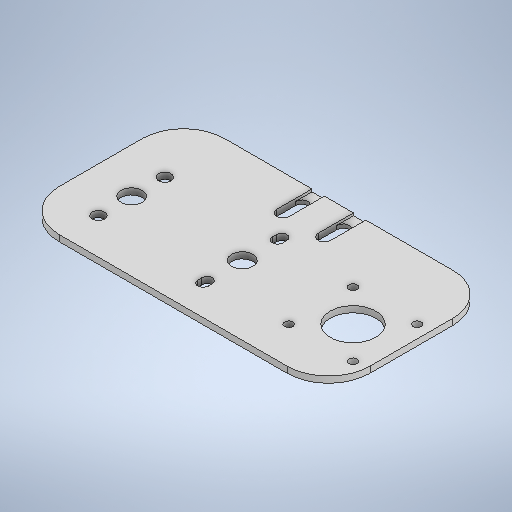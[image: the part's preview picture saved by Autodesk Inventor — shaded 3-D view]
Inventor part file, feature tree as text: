
AUTODESK INVENTOR PART (.ipt)
format: ipt  version: 2025.2 (Build 292293000, 293)  size: 341,504 bytes
history: native  units: mm
features: extrude x5, sketch x4, fillet x1
ambient origin geometry x8: Origin, YZ Plane, XZ Plane, XY Plane, X Axis, Y Axis, Z Axis, Center Point
bodies: Solid1 (feature_tree)
feature tree (10):
  extrude  "Extrusion1"  Depth=80.0mm
  sketch  "Sketch4"  dims[d2=3.0mm d3=0.0mm d14=20.0mm]
  extrude  "Extrusion3"  Depth=20.0mm
  extrude  "Extrusion4"  Depth=6.0mm
  extrude  "Extrusion5"  Depth=5.0mm
  extrude  "Extrusion6"  Depth=5.0mm
  fillet  "Fillet1"  Radius=3.0mm
  sketch  "Sketch1"  dims[d0=150.0mm d1=80.0mm]
  sketch  "Sketch5"  dims[d15=20.0mm d16=6.0mm]
  sketch  "Sketch6"  dims[d17=6.0mm d18=5.0mm d19=5.0mm d20=3.0mm d21=3.0mm d22=3.0mm d23=3.0mm d24=0.0mm d25=0.0mm d26=25.0mm d36=0.0mm d37=0.0mm d38=1.2mm d39=0.0mm d49=150.0mm d50=43.2mm d51=43.2mm d52=22.0mm d53=31.0mm d54=31.0mm d55=4.0mm d56=4.0mm d57=4.0mm d58=4.0mm d59=25.0mm d60=43.2mm d61=43.2mm d62=43.2mm d63=10.2mm d64=43.2mm d65=53.4mm d66=10.2mm d67=0.0mm d68=0.0mm d69=38.0mm d70=5.0mm d71=2.0mm d72=5.0mm d73=5.0mm d74=2.0mm d75=5.0mm d84=32.0mm d85=6.0mm d86=6.0mm d87=20.0mm d27=0.872665mm d28=0.5mm d29=0.872665mm]
